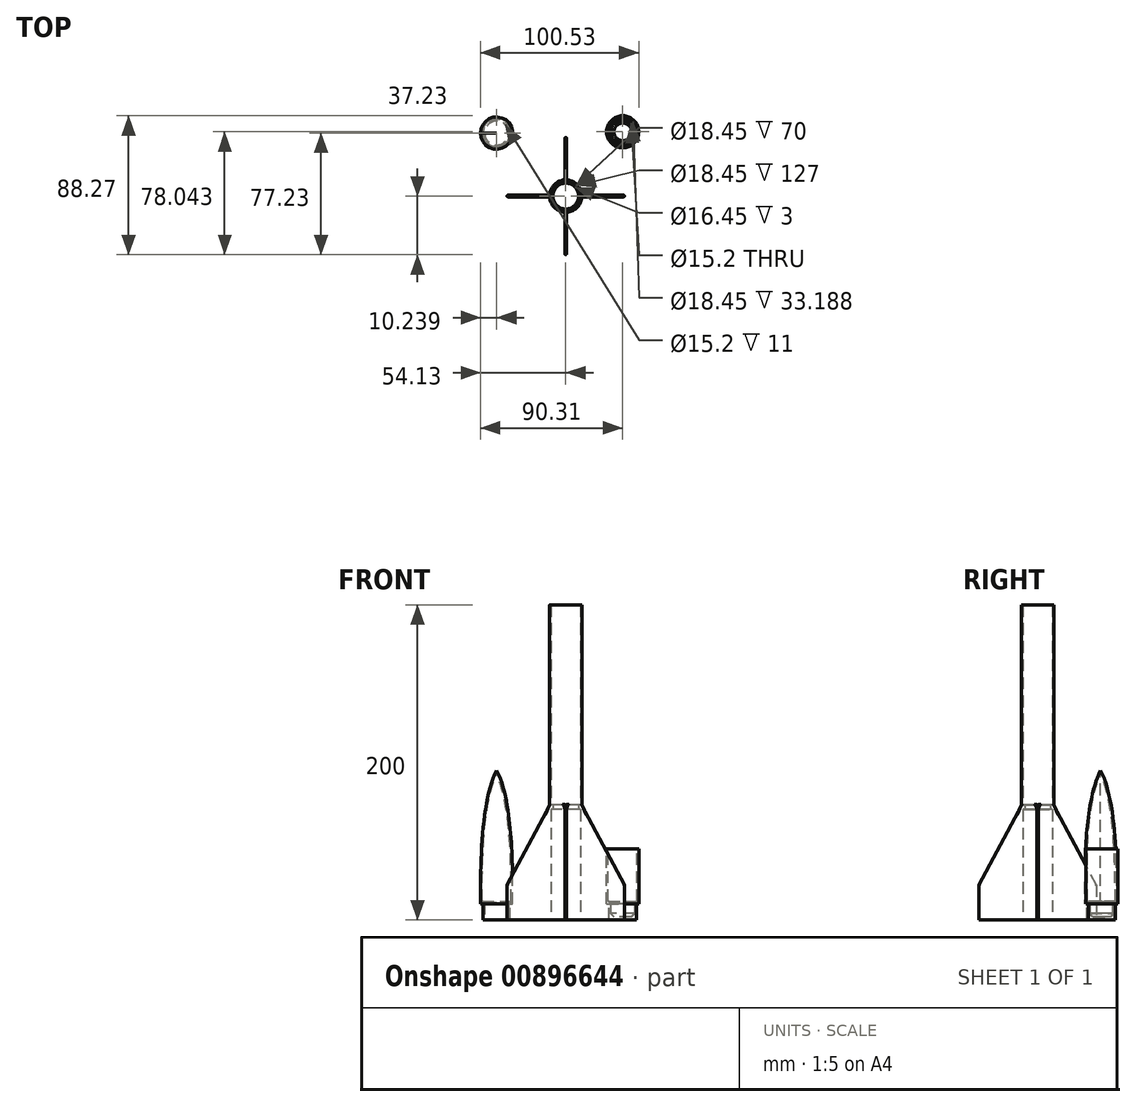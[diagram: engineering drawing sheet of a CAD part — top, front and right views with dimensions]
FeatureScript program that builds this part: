
annotation { "Feature Type Name" : "Feature", "Feature Type Description" : "" }
export const myFeature = defineFeature(function(context is Context, id is Id, definition is map)
    precondition{}
    {
        {
            var Q0;
            Q0=qCreatedBy(makeId("Top.planeOp"),FACE);
            var sketch = newSketch(context, id + "F0", { "sketchPlane" : qUnion([Q0])});
            skCircle(sketch, "E0", {"center": v(0, 0) * mm, "radius": 10.23 * mm});
            skCircle(sketch, "E1", {"center": v(0, 0) * mm, "radius": 9.23 * mm});
            skSolve(sketch);
        }
        {
            var Q0;
            Q0 = qSketchRegion(id + "F0", true);
            extrude(context, id + "F1", {"entities" : qUnion([Q0]), "depth" : 200 * mm, "offsetDistance" : 25 * mm});
        }
        {
            var Q0;
            Q0=qCreatedBy(makeId("Front.planeOp"),FACE);
            var sketch = newSketch(context, id + "F2", { "sketchPlane" : qUnion([Q0])});
            skLineSegment(sketch, "E2", {"start": v(4.72, 83.45) * mm, "end": v(37.23, 22.5) * mm});
            skLineSegment(sketch, "E3", {"start": v(37.23, 0) * mm, "end": v(4.72, 0) * mm});
            skLineSegment(sketch, "E4", {"start": v(37.23, 0) * mm, "end": v(37.23, 22.5) * mm});
            skPoint(sketch, "E5.orphan", {"position": v(49.23, 0) * mm});
            skLineSegment(sketch, "E6", {"start": v(4.72, 83.45) * mm, "end": v(4.72, 0) * mm});
            skLineSegment(sketch, "E7.0", {"start": v(-10.23, 0) * mm, "end": v(10.23, 0) * mm, "construction": true});
            skSolve(sketch);
        }
        {
            var Q0;
            Q0 = qSketchRegion(id + "F2", true);
            extrude(context, id + "F3", {"entities" : qUnion([Q0]), "operationType" : NewBodyOperationType.ADD, "endBound" : BoundingType.SYMMETRIC, "depth" : 1 * mm, "offsetDistance" : 25 * mm});
        }
        {
            var Q0;
            Q0=makeQuery(id+"F3.boolean.opBoolean","INTERSECT",EDGE,{"derivedFrom":[makeQuery(id+"F1.opExtrude","SWEPT_FACE",FACE,{"disambiguationData":[OSD([sQuery(id+"F0.wireOp",EDGE,"E0")])]}),makeQuery(id+"F3.opExtrude","CAP_FACE",FACE,{"disambiguationData":[OSD([sQuery(id+"F2.wireOp",EDGE,"E2"),sQuery(id+"F2.wireOp",EDGE,"E3"),sQuery(id+"F2.wireOp",EDGE,"E4"),sQuery(id+"F2.wireOp",EDGE,"E6")])],"isStart":true})]});
            var Q1;
            Q1=makeQuery(id+"F3.boolean.opBoolean","INTERSECT",EDGE,{"derivedFrom":[makeQuery(id+"F1.opExtrude","SWEPT_FACE",FACE,{"disambiguationData":[OSD([sQuery(id+"F0.wireOp",EDGE,"E0")])]}),makeQuery(id+"F3.opExtrude","CAP_FACE",FACE,{"disambiguationData":[OSD([sQuery(id+"F2.wireOp",EDGE,"E2"),sQuery(id+"F2.wireOp",EDGE,"E3"),sQuery(id+"F2.wireOp",EDGE,"E4"),sQuery(id+"F2.wireOp",EDGE,"E6")])],"isStart":false})]});
            fillet(context, id + "F4", {"entities" : qUnion([Q0, Q1]), "radius" : 2 * mm, "tangentPropagation" : true, "allowEdgeOverflow" : false});
        }
        {
            var Q0;
            {var subQ0=makeQuery(id+"F1.opExtrude","SWEPT_FACE",FACE,{"disambiguationData":[OSD([sQuery(id+"F0.wireOp",EDGE,"E0")])]});var subQ1=sQuery(id+"F2.wireOp",EDGE,"E6");var subQ2=sQuery(id+"F2.wireOp",EDGE,"E4");var subQ3=sQuery(id+"F2.wireOp",EDGE,"E3");var subQ4=sQuery(id+"F2.wireOp",EDGE,"E2");var subQ5=makeQuery(id+"F3.opExtrude","CAP_FACE",FACE,{"disambiguationData":[OSD([subQ4,subQ3,subQ2,subQ1])],"isStart":false});Q0=makeQuery(id+"F4.opFillet","BLEND_EDGE",EDGE,{"blendedFrom":[makeQuery(id+"F3.boolean.opBoolean","INTERSECT",EDGE,{"derivedFrom":[subQ0,subQ5]}),makeQuery(id+"F3.boolean.opBoolean","SPLIT",FACE,{"disambiguationData":[TD([subQ0])],"derivedFrom":makeQuery(id+"F3.opExtrude","SWEPT_FACE",FACE,{"disambiguationData":[OSD([subQ4])]})})],"blendedInto":[makeQuery(id+"F3.boolean.opBoolean","SPLIT",FACE,{"disambiguationData":[TD([subQ0])],"derivedFrom":makeQuery(id+"F3.opExtrude","SWEPT_FACE",FACE,{"disambiguationData":[OSD([subQ4])]})})]});}
            var Q1;
            {var subQ0=makeQuery(id+"F1.opExtrude","SWEPT_FACE",FACE,{"disambiguationData":[OSD([sQuery(id+"F0.wireOp",EDGE,"E0")])]});var subQ1=sQuery(id+"F2.wireOp",EDGE,"E6");var subQ2=sQuery(id+"F2.wireOp",EDGE,"E4");var subQ3=sQuery(id+"F2.wireOp",EDGE,"E3");var subQ4=sQuery(id+"F2.wireOp",EDGE,"E2");var subQ5=makeQuery(id+"F3.opExtrude","CAP_FACE",FACE,{"disambiguationData":[OSD([subQ4,subQ3,subQ2,subQ1])],"isStart":true});Q1=makeQuery(id+"F4.opFillet","BLEND_EDGE",EDGE,{"blendedFrom":[makeQuery(id+"F3.boolean.opBoolean","INTERSECT",EDGE,{"derivedFrom":[subQ0,subQ5]}),makeQuery(id+"F3.boolean.opBoolean","SPLIT",FACE,{"disambiguationData":[TD([subQ0])],"derivedFrom":makeQuery(id+"F3.opExtrude","SWEPT_FACE",FACE,{"disambiguationData":[OSD([subQ4])]})})],"blendedInto":[makeQuery(id+"F3.boolean.opBoolean","SPLIT",FACE,{"disambiguationData":[TD([subQ0])],"derivedFrom":makeQuery(id+"F3.opExtrude","SWEPT_FACE",FACE,{"disambiguationData":[OSD([subQ4])]})})]});}
            chamfer(context, id + "F5", {"entities" : qUnion([Q0, Q1]), "width" : .5 * mm, "tangentPropagation" : true});
        }
        {
            var Q0;
            Q0=makeQuery(id+"F3.opExtrude","CAP_EDGE",EDGE,{"disambiguationData":[OSD([sQuery(id+"F2.wireOp",EDGE,"E4")])],"isStart":false});
            var Q1;
            Q1=makeQuery(id+"F3.opExtrude","CAP_EDGE",EDGE,{"disambiguationData":[OSD([sQuery(id+"F2.wireOp",EDGE,"E4")])],"isStart":true});
            var Q2;
            {var subQ0=sQuery(id+"F2.wireOp",EDGE,"E2");var subQ2=sQuery(id+"F0.wireOp",EDGE,"E0");var subQ3=sQuery(id+"F2.wireOp",EDGE,"E3");var subQ4=makeQuery(id+"F1.opExtrude","SWEPT_FACE",FACE,{"disambiguationData":[OSD([subQ2])]});var subQ5=sQuery(id+"F2.wireOp",EDGE,"E4");var subQ7=makeQuery(id+"F3.opExtrude","CAP_FACE",FACE,{"disambiguationData":[OSD([subQ0,subQ3,subQ5,sQuery(id+"F2.wireOp",EDGE,"E6")])],"isStart":false});Q2=makeQuery(id+"F5.opChamfer","BLEND_EDGE",EDGE,{"blendedFrom":[makeQuery(id+"F3.boolean.opBoolean","SPLIT",EDGE,{"disambiguationData":[TD([subQ4])],"derivedFrom":makeQuery(id+"F3.opExtrude","CAP_EDGE",EDGE,{"disambiguationData":[OSD([subQ0])],"isStart":false})}),makeQuery(id+"F3.boolean.opBoolean","SPLIT",FACE,{"disambiguationData":[TD([subQ4])],"derivedFrom":subQ7})],"blendedInto":[makeQuery(id+"F3.boolean.opBoolean","SPLIT",FACE,{"disambiguationData":[TD([subQ4])],"derivedFrom":subQ7})]});}
            var Q3;
            {var subQ0=sQuery(id+"F2.wireOp",EDGE,"E2");var subQ2=sQuery(id+"F0.wireOp",EDGE,"E0");var subQ3=sQuery(id+"F2.wireOp",EDGE,"E3");var subQ4=makeQuery(id+"F1.opExtrude","SWEPT_FACE",FACE,{"disambiguationData":[OSD([subQ2])]});var subQ5=sQuery(id+"F2.wireOp",EDGE,"E4");var subQ7=makeQuery(id+"F3.opExtrude","CAP_FACE",FACE,{"disambiguationData":[OSD([subQ0,subQ3,subQ5,sQuery(id+"F2.wireOp",EDGE,"E6")])],"isStart":true});Q3=makeQuery(id+"F5.opChamfer","BLEND_EDGE",EDGE,{"blendedFrom":[makeQuery(id+"F3.boolean.opBoolean","SPLIT",EDGE,{"disambiguationData":[TD([subQ4])],"derivedFrom":makeQuery(id+"F3.opExtrude","CAP_EDGE",EDGE,{"disambiguationData":[OSD([subQ0])],"isStart":true})}),makeQuery(id+"F3.boolean.opBoolean","SPLIT",FACE,{"disambiguationData":[TD([subQ4])],"derivedFrom":subQ7})],"blendedInto":[makeQuery(id+"F3.boolean.opBoolean","SPLIT",FACE,{"disambiguationData":[TD([subQ4])],"derivedFrom":subQ7})]});}
            fillet(context, id + "F6", {"entities" : qUnion([Q0, Q1, Q2, Q3]), "radius" : .5 * mm, "tangentPropagation" : true, "allowEdgeOverflow" : false});
        }
        {
            var Q0;
            {var subQ0=makeQuery(id+"F1.opExtrude","SWEPT_FACE",FACE,{"disambiguationData":[OSD([sQuery(id+"F0.wireOp",EDGE,"E0")])]});var subQ4=sQuery(id+"F2.wireOp",EDGE,"E2");Q0=makeQuery(id+"F5.opChamfer","BLEND_EDGE",EDGE,{"blendedFrom":[makeQuery(id+"F3.boolean.opBoolean","SPLIT",EDGE,{"disambiguationData":[TD([subQ0])],"derivedFrom":makeQuery(id+"F3.opExtrude","CAP_EDGE",EDGE,{"disambiguationData":[OSD([subQ4])],"isStart":true})}),makeQuery(id+"F3.boolean.opBoolean","SPLIT",EDGE,{"disambiguationData":[TD([subQ0])],"derivedFrom":makeQuery(id+"F3.opExtrude","CAP_EDGE",EDGE,{"disambiguationData":[OSD([subQ4])],"isStart":false})})],"blendedInto":[]});}
            var Q1;
            {var subQ0=makeQuery(id+"F1.opExtrude","SWEPT_FACE",FACE,{"disambiguationData":[OSD([sQuery(id+"F0.wireOp",EDGE,"E0")])]});var subQ1=sQuery(id+"F2.wireOp",EDGE,"E6");var subQ2=sQuery(id+"F2.wireOp",EDGE,"E4");var subQ3=sQuery(id+"F2.wireOp",EDGE,"E3");var subQ4=sQuery(id+"F2.wireOp",EDGE,"E2");var subQ5=makeQuery(id+"F3.opExtrude","CAP_FACE",FACE,{"disambiguationData":[OSD([subQ4,subQ3,subQ2,subQ1])],"isStart":false});var subQ6=makeQuery(id+"F3.opExtrude","CAP_FACE",FACE,{"disambiguationData":[OSD([subQ4,subQ3,subQ2,subQ1])],"isStart":true});var subQ7=makeQuery(id+"F3.boolean.opBoolean","SPLIT",FACE,{"disambiguationData":[TD([subQ0])],"derivedFrom":makeQuery(id+"F3.opExtrude","SWEPT_FACE",FACE,{"disambiguationData":[OSD([subQ4])]})});Q1=makeQuery(id+"F5.opChamfer","BLEND_EDGE",EDGE,{"blendedFrom":[makeQuery(id+"F4.opFillet","BLEND_EDGE",EDGE,{"blendedFrom":[makeQuery(id+"F3.boolean.opBoolean","INTERSECT",EDGE,{"derivedFrom":[subQ0,subQ6]}),subQ7],"blendedInto":[subQ7]}),makeQuery(id+"F4.opFillet","BLEND_EDGE",EDGE,{"blendedFrom":[makeQuery(id+"F3.boolean.opBoolean","INTERSECT",EDGE,{"derivedFrom":[subQ0,subQ5]}),subQ7],"blendedInto":[subQ7]})],"blendedInto":[]});}
            fillet(context, id + "F7", {"entities" : qUnion([Q0, Q1]), "radius" : .5 * mm, "tangentPropagation" : true, "allowEdgeOverflow" : false});
        }
        {
            var Q0;
            Q0=makeQuery(id+"F1.opExtrude","SWEPT_BODY",BODY,{"disambiguationData":[OSD([sQuery(id+"F0.wireOp",EDGE,"E0"),sQuery(id+"F0.wireOp",EDGE,"E1")])]});
            var Q1;
            Q1=makeQuery(id+"F1.opExtrude","SWEPT_FACE",FACE,{"disambiguationData":[OSD([sQuery(id+"F0.wireOp",EDGE,"E1")])]});
            circularPattern(context, id + "F8", {"entities" : qUnion([Q0]), "axis" : qUnion([Q1]), "angle" : 360 * degree, "instanceCount" : 4, "equalSpace" : true});
        }
        {
            var Q0;
            Q0=makeQuery(id+"F3.boolean.opBoolean","MERGE",FACE,{"derivedFrom":[makeQuery(id+"F1.opExtrude","CAP_FACE",FACE,{"disambiguationData":[OSD([sQuery(id+"F0.wireOp",EDGE,"E0"),sQuery(id+"F0.wireOp",EDGE,"E1")])],"isStart":true}),makeQuery(id+"F3.opExtrude","SWEPT_FACE",FACE,{"disambiguationData":[OSD([sQuery(id+"F2.wireOp",EDGE,"E3")])]})]});
            var sketch = newSketch(context, id + "F9", { "sketchPlane" : qUnion([Q0])});
            skArc(sketch, "E8.0", {"start": v(9.21, -0.5) * mm, "mid": v(-9.22, 0) * mm, "end": v(9.21, 0.5) * mm});
            skArc(sketch, "E9.0", {"start": v(-0.5, -9.21) * mm, "mid": v(0, 9.22) * mm, "end": v(0.5, -9.21) * mm});
            skSolve(sketch);
        }
        {
            var Q0;
            Q0 = qSketchRegion(id + "F9", true);
            extrude(context, id + "F10", {"entities" : qUnion([Q0]), "operationType" : NewBodyOperationType.REMOVE, "endBound" : BoundingType.THROUGH_ALL, "oppositeDirection" : true, "depth" : 25 * mm, "offsetDistance" : 25 * mm});
        }
        {
            var Q0;
            Q0=qCreatedBy(makeId("Top.planeOp"),FACE);
            var sketch = newSketch(context, id + "F11", { "sketchPlane" : qUnion([Q0])});
            skCircle(sketch, "E10", {"center": v(36.18, 39.19) * mm, "radius": 9.23 * mm});
            skCircle(sketch, "E11.0", {"center": v(36.18, 39.19) * mm, "radius": 10.23 * mm});
            skSolve(sketch);
        }
        {
            var Q0;
            Q0 = qSketchRegion(id + "F11", true);
            extrude(context, id + "F12", {"entities" : qUnion([Q0]), "depth" : 35 * mm, "offsetDistance" : 25 * mm});
        }
        {
            var Q0;
            Q0=makeQuery(id+"F12.opExtrude","CAP_FACE",FACE,{"disambiguationData":[OSD([sQuery(id+"F11.wireOp",EDGE,"E10"),sQuery(id+"F11.wireOp",EDGE,"E11.0")])],"isStart":false});
            var sketch = newSketch(context, id + "F13", { "sketchPlane" : qUnion([Q0])});
            skCircle(sketch, "E12", {"center": v(36.18, 39.19) * mm, "radius": 7.6 * mm});
            skCircle(sketch, "E13", {"center": v(36.18, 39.19) * mm, "radius": 9.23 * mm});
            skSolve(sketch);
        }
        {
            var Q0;
            Q0 = qSketchRegion(id + "F13", true);
            extrude(context, id + "F14", {"entities" : qUnion([Q0]), "operationType" : NewBodyOperationType.ADD, "oppositeDirection" : true, "depth" : 2 * mm, "offsetDistance" : 25 * mm});
        }
        {
            var Q0;
            Q0=makeQuery(id+"F14.opExtrude","CAP_EDGE",EDGE,{"disambiguationData":[OSD([sQuery(id+"F13.wireOp",EDGE,"E12")])],"isStart":false});
            chamfer(context, id + "F15", {"entities" : qUnion([Q0]), "chamferType" : ChamferType.TWO_OFFSETS, "width1" : 2 * mm, "oppositeDirection" : false, "width2" : 1 * mm, "tangentPropagation" : true});
        }
        {
            var Q0;
            Q0=makeQuery(id+"F14.boolean.opBoolean","MERGE",FACE,{"derivedFrom":[makeQuery(id+"F12.opExtrude","CAP_FACE",FACE,{"disambiguationData":[OSD([sQuery(id+"F11.wireOp",EDGE,"E10"),sQuery(id+"F11.wireOp",EDGE,"E11.0")])],"isStart":false}),makeQuery(id+"F14.opExtrude","CAP_FACE",FACE,{"disambiguationData":[OSD([sQuery(id+"F13.wireOp",EDGE,"E12"),sQuery(id+"F13.wireOp",EDGE,"E13")])],"isStart":true})]});
            var sketch = newSketch(context, id + "F16", { "sketchPlane" : qUnion([Q0])});
            skCircle(sketch, "E14", {"center": v(36.18, 39.19) * mm, "radius": 7.6 * mm});
            skCircle(sketch, "E15", {"center": v(36.18, 39.19) * mm, "radius": 8.6 * mm});
            skSolve(sketch);
        }
        {
            var Q0;
            Q0 = qSketchRegion(id + "F16", true);
            extrude(context, id + "F17", {"entities" : qUnion([Q0]), "operationType" : NewBodyOperationType.ADD, "depth" : 10 * mm, "offsetDistance" : 25 * mm});
        }
        {
            var Q0;
            Q0=makeQuery(id+"F17.opExtrude","CAP_FACE",FACE,{"disambiguationData":[OSD([sQuery(id+"F16.wireOp",EDGE,"E14"),sQuery(id+"F16.wireOp",EDGE,"E15")])],"isStart":false});
            var sketch = newSketch(context, id + "F18", { "sketchPlane" : qUnion([Q0])});
            skCircle(sketch, "E16.0", {"center": v(36.18, 39.19) * mm, "radius": 8.6 * mm});
            skSolve(sketch);
        }
        {
            var Q0;
            Q0 = qSketchRegion(id + "F18", true);
            extrude(context, id + "F19", {"entities" : qUnion([Q0]), "operationType" : NewBodyOperationType.ADD, "oppositeDirection" : true, "depth" : 2 * mm, "offsetDistance" : 25 * mm});
        }
        {
            var Q0;
            Q0=makeQuery(id+"F19.boolean.opBoolean","INTERSECT",EDGE,{"derivedFrom":[makeQuery(id+"F17.boolean.opBoolean","MERGE",FACE,{"derivedFrom":[makeQuery(id+"F14.opExtrude","SWEPT_FACE",FACE,{"disambiguationData":[OSD([sQuery(id+"F13.wireOp",EDGE,"E12")])]}),makeQuery(id+"F17.opExtrude","SWEPT_FACE",FACE,{"disambiguationData":[OSD([sQuery(id+"F16.wireOp",EDGE,"E14")])]})]}),makeQuery(id+"F19.opExtrude","CAP_FACE",FACE,{"disambiguationData":[OSD([sQuery(id+"F18.wireOp",EDGE,"E16.0")])],"isStart":false})]});
            chamfer(context, id + "F20", {"entities" : qUnion([Q0]), "width" : 2 * mm, "tangentPropagation" : true});
        }
        {
            var Q0;
            Q0=qCreatedBy(makeId("Front.planeOp"),FACE);
            cPlane(context, id + "F21", {"entities" : qUnion([Q0]), "cplaneType" : CPlaneType.OFFSET, "offset" : 40 * mm, "oppositeDirection" : true, "width" : 150 * mm, "height" : 150 * mm});
        }
        {
            var Q0;
            Q0=qCreatedBy(id+"F21.planeOp",FACE);
            var sketch = newSketch(context, id + "F22", { "sketchPlane" : qUnion([Q0])});
            skLineSegment(sketch, "E17", {"start": v(-33.67, 0) * mm, "end": v(-54.12, 0) * mm, "construction": true});
            skLineSegment(sketch, "E18", {"start": v(-43.9, 0) * mm, "end": v(-43.9, 85) * mm, "construction": true});
            skFitSpline(sketch, "E19", {"points": [v(-54.12, 0) * mm, v(-43.9, 85) * mm], "startDerivative": vector(-0.41, 89.64) * mm, "endDerivative": vector(28.5, 55.17) * mm});
            skLineSegment(sketch, "E20", {"start": v(-43.9, 85) * mm, "end": v(-43.9, 0) * mm});
            skLineSegment(sketch, "E21", {"start": v(-43.9, 0) * mm, "end": v(-54.12, 0) * mm});
            skSolve(sketch);
        }
        {
            var Q0;
            Q0 = qSketchRegion(id + "F22", true);
            var Q1;
            Q1=sQuery(id+"F22.wireOp",EDGE,"E20");
            revolve(context, id + "F23", {"surfaceOperationType" : NewSurfaceOperationType.NEW, "entities" : qUnion([Q0]), "axis" : qUnion([Q1]), "revolveType" : RevolveType.FULL});
        }
        {
            var Q0;
            Q0=makeQuery(id+"F23.opRevolve","SWEPT_FACE",FACE,{"disambiguationData":[OSD([sQuery(id+"F22.wireOp",EDGE,"E21")])]});
            shell(context, id + "F24", {"entities" : qUnion([Q0]), "thickness" : 1 * mm});
        }
        {
            var Q0;
            Q0=makeQuery(id+"F23.opRevolve","SWEPT_FACE",FACE,{"disambiguationData":[OSD([sQuery(id+"F22.wireOp",EDGE,"E21")])]});
            var sketch = newSketch(context, id + "F25", { "sketchPlane" : qUnion([Q0])});
            skCircle(sketch, "E22", {"center": v(-43.9, -40) * mm, "radius": 7.6 * mm});
            skCircle(sketch, "E23.0", {"center": v(-43.9, -40) * mm, "radius": 10.22 * mm});
            skSolve(sketch);
        }
        {
            var Q0;
            Q0 = qSketchRegion(id + "F25", true);
            extrude(context, id + "F26", {"entities" : qUnion([Q0]), "operationType" : NewBodyOperationType.ADD, "oppositeDirection" : true, "depth" : 2 * mm, "offsetDistance" : 25 * mm});
        }
        {
            var Q0;
            Q0=makeQuery(id+"F26.opExtrude","CAP_EDGE",EDGE,{"disambiguationData":[OSD([sQuery(id+"F25.wireOp",EDGE,"E22")])],"isStart":false});
            chamfer(context, id + "F27", {"entities" : qUnion([Q0]), "chamferType" : ChamferType.TWO_OFFSETS, "width1" : 2 * mm, "oppositeDirection" : false, "width2" : 1 * mm, "tangentPropagation" : true});
        }
        {
            var Q0;
            Q0=makeQuery(id+"F26.boolean.opBoolean","MERGE",FACE,{"derivedFrom":[makeQuery(id+"F23.opRevolve","SWEPT_FACE",FACE,{"disambiguationData":[OSD([sQuery(id+"F22.wireOp",EDGE,"E21")])]}),makeQuery(id+"F26.opExtrude","CAP_FACE",FACE,{"disambiguationData":[OSD([sQuery(id+"F25.wireOp",EDGE,"E22"),sQuery(id+"F25.wireOp",EDGE,"E23.0")])],"isStart":true})]});
            var sketch = newSketch(context, id + "F28", { "sketchPlane" : qUnion([Q0])});
            skCircle(sketch, "E24", {"center": v(-43.9, -40) * mm, "radius": 7.6 * mm});
            skCircle(sketch, "E25.0", {"center": v(-43.9, -40) * mm, "radius": 8.6 * mm});
            skSolve(sketch);
        }
        {
            var Q0;
            Q0 = qSketchRegion(id + "F28", true);
            extrude(context, id + "F29", {"entities" : qUnion([Q0]), "operationType" : NewBodyOperationType.ADD, "depth" : 10 * mm, "offsetDistance" : 25 * mm});
        }
        {
            var Q0;
            Q0=makeQuery(id+"F23.opRevolve","SWEPT_BODY",BODY,{"disambiguationData":[OSD([sQuery(id+"F22.wireOp",EDGE,"E19"),sQuery(id+"F22.wireOp",EDGE,"E20"),sQuery(id+"F22.wireOp",EDGE,"E21")])]});
            transform(context, id + "F30", {"entities" : qUnion([Q0]), "transformType" : TransformType.TRANSLATION_3D, "dx" : 0 * mm, "dy" : 0 * mm, "dz" : 10 * mm, "makeCopy" : false});
        }
        {
            var Q0;
            Q0=qCreatedBy(makeId("Top.planeOp"),FACE);
            cPlane(context, id + "F31", {"entities" : qUnion([Q0]), "cplaneType" : CPlaneType.OFFSET, "offset" : 70 * mm, "width" : 150 * mm, "height" : 150 * mm});
        }
        {
            var Q0;
            Q0=qCreatedBy(id+"F31.planeOp",FACE);
            var sketch = newSketch(context, id + "F32", { "sketchPlane" : qUnion([Q0])});
            skCircle(sketch, "E26", {"center": v(0, 0) * mm, "radius": 8.22 * mm});
            skCircle(sketch, "E27.0", {"center": v(0, 0) * mm, "radius": 10.23 * mm});
            skSolve(sketch);
        }
        {
            var Q0;
            Q0 = qSketchRegion(id + "F32", true);
            extrude(context, id + "F33", {"entities" : qUnion([Q0]), "operationType" : NewBodyOperationType.ADD, "depth" : 3 * mm, "offsetDistance" : 25 * mm});
        }
        {
            var Q0;
            Q0=qCreatedBy(id+"F21.planeOp",FACE);
            var sketch = newSketch(context, id + "F34", { "sketchPlane" : qUnion([Q0])});
            skLineSegment(sketch, "E28.0", {"start": v(27.58, 45) * mm, "end": v(44.78, 45) * mm});
            skLineSegment(sketch, "E29.0", {"start": v(25.95, 0) * mm, "end": v(46.4, 0) * mm});
            skLineSegment(sketch, "E30", {"start": v(36.18, 45) * mm, "end": v(36.18, 0) * mm});
            skLineSegment(sketch, "E31", {"start": v(35.45, 22.5) * mm, "end": v(55.94, 22.5) * mm});
            skPoint(sketch, "E31.startSnap0", {"position": v(36.18, 22.5) * mm});
            skSolve(sketch);
        }
        {
            var Q0;
            Q0=makeQuery(id+"F12.opExtrude","SWEPT_BODY",BODY,{"disambiguationData":[OSD([sQuery(id+"F11.wireOp",EDGE,"E10"),sQuery(id+"F11.wireOp",EDGE,"E11.0")])]});
            var Q1;
            Q1=sQuery(id+"F34.wireOp",EDGE,"E31");
            transform(context, id + "F35", {"entities" : qUnion([Q0]), "transformType" : TransformType.ROTATION, "transformAxis" : qUnion([Q1]), "angle" : 180 * degree, "makeCopy" : false});
        }
    });
